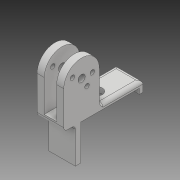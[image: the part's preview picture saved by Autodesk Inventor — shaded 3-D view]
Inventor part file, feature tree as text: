
AUTODESK INVENTOR PART (.ipt)
format: ipt  version: 2018 (Build 220112000, 112)  size: 200,192 bytes
history: native  units: mm
features: extrude x6, sketch x6, other x1, fillet x1
ambient origin geometry x8: Origin, YZ Plane, XZ Plane, XY Plane, X Axis, Y Axis, Z Axis, Center Point
bodies: Body1 (feature_tree)
feature tree (14):
  other  "Sólido1"
  extrude  "Extrusión1"  Depth=15.0mm
  sketch  "Boceto2"  dims[d2=3.0mm d3=0.0mm d9=6.5mm]
  sketch  "Boceto4"  dims[d10=6.0mm d11=3.0mm]
  extrude  "Extrusión3"  Depth=6.5mm
  extrude  "Extrusión4"  Depth=3.0mm
  extrude  "Extrusión5"  Depth=4.0mm
  extrude  "Extrusión6"  Depth=4.0mm TaperAngle=0.0deg
  extrude  "Extrusión7"  Depth=2.0mm TaperAngle=0.0deg
  fillet  "Empalme1"  Radius=2.0mm
  sketch  "Boceto1"  dims[d0=33.0mm d1=15.0mm]
  sketch  "Boceto5"  dims[d12=20.0mm d13=4.0mm]
  sketch  "Boceto6"  dims[d14=4.0mm d15=28.0mm d16=0.0mm]
  sketch  "Boceto7"  dims[d17=3.0mm d18=0.0mm d19=3.0mm d20=0.0mm d21=2.0mm d22=6.0mm d23=3.0mm d24=20.0mm d25=3.0mm d26=0.0mm d28=4.0mm d29=2.5mm d30=4.0mm d34=4.0mm d35=4.0mm d36=2.5mm d37=2.5mm d38=3.0mm d39=0.0mm d40=2.0mm]
